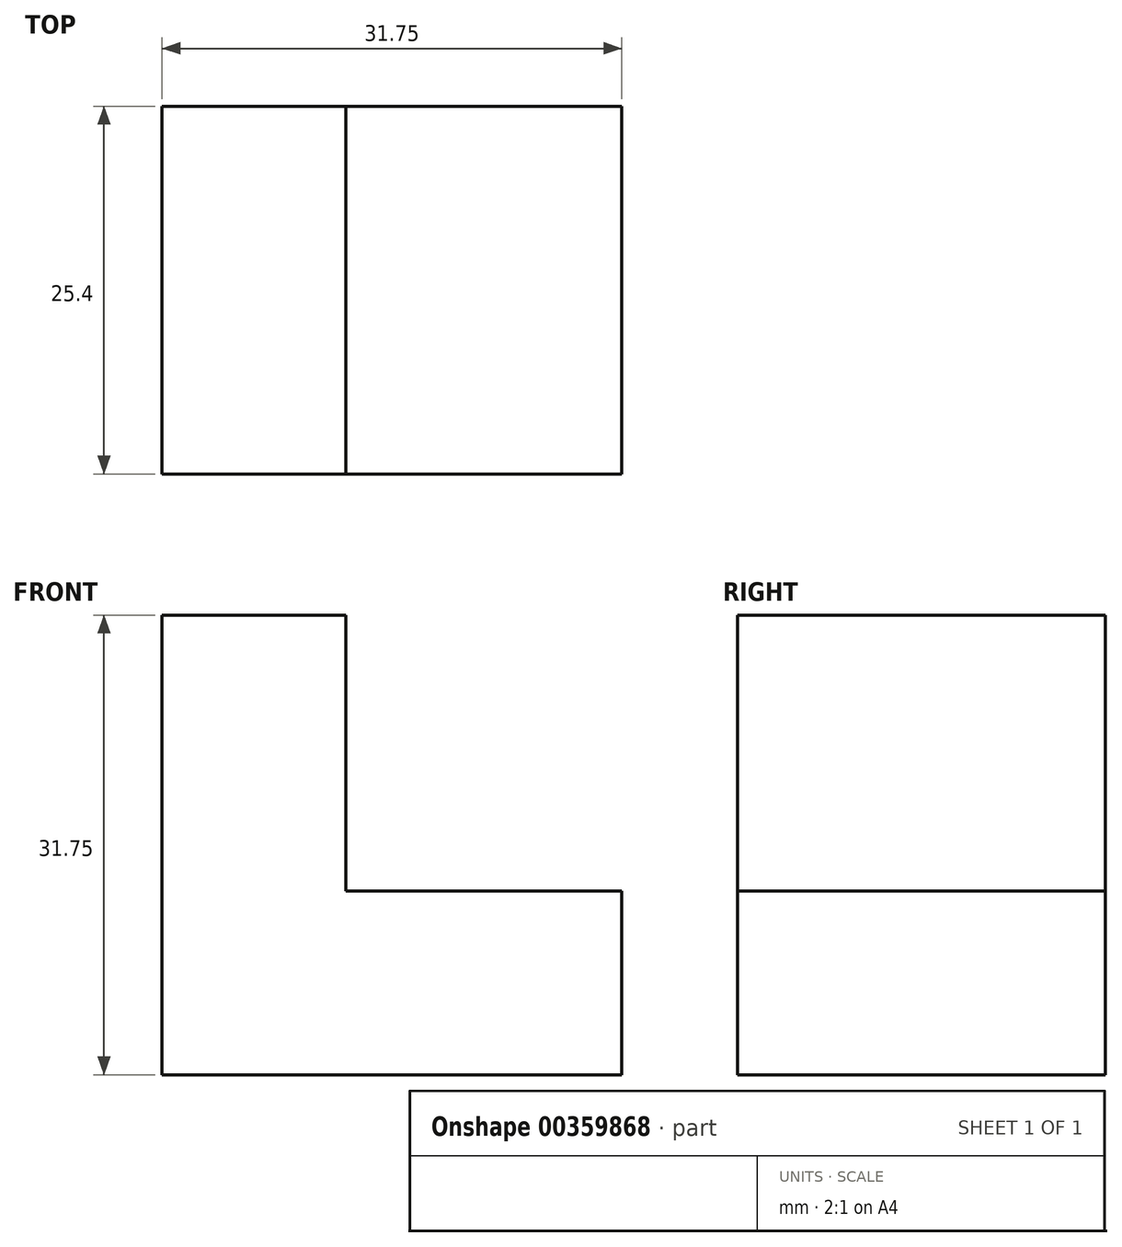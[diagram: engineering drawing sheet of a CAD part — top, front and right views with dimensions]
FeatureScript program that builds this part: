
annotation { "Feature Type Name" : "Feature", "Feature Type Description" : "" }
export const myFeature = defineFeature(function(context is Context, id is Id, definition is map)
    precondition{}
    {
        {
            var Q0;
            Q0=qCreatedBy(makeId("Front.planeOp"),FACE);
            var sketch = newSketch(context, id + "F0", { "sketchPlane" : qUnion([Q0])});
            skSolve(sketch);
        }
        {
            var Q0;
            Q0=qCreatedBy(makeId("Front.planeOp"),FACE);
            var sketch = newSketch(context, id + "F1", { "sketchPlane" : qUnion([Q0])});
            skLineSegment(sketch, "E0", {"start": v(0, 0) * mm, "end": v(31.75, 0) * mm});
            skLineSegment(sketch, "E1", {"start": v(31.75, 0) * mm, "end": v(31.75, 12.7) * mm});
            skLineSegment(sketch, "E2", {"start": v(31.75, 12.7) * mm, "end": v(12.7, 12.7) * mm});
            skLineSegment(sketch, "E3", {"start": v(12.7, 12.7) * mm, "end": v(12.7, 31.75) * mm});
            skLineSegment(sketch, "E4", {"start": v(12.7, 31.75) * mm, "end": v(0, 31.75) * mm});
            skLineSegment(sketch, "E5", {"start": v(0, 31.75) * mm, "end": v(0, 0) * mm});
            skSolve(sketch);
        }
        {
            var Q0;
            Q0 = qSketchRegion(id + "F1", true);
            var Q1;
            Q1 = qSketchRegion(id + "F0", true);
            extrude(context, id + "F2", {"entities" : qUnion([Q0, Q1]), "depth" : 25.4 * mm});
        }
    });
